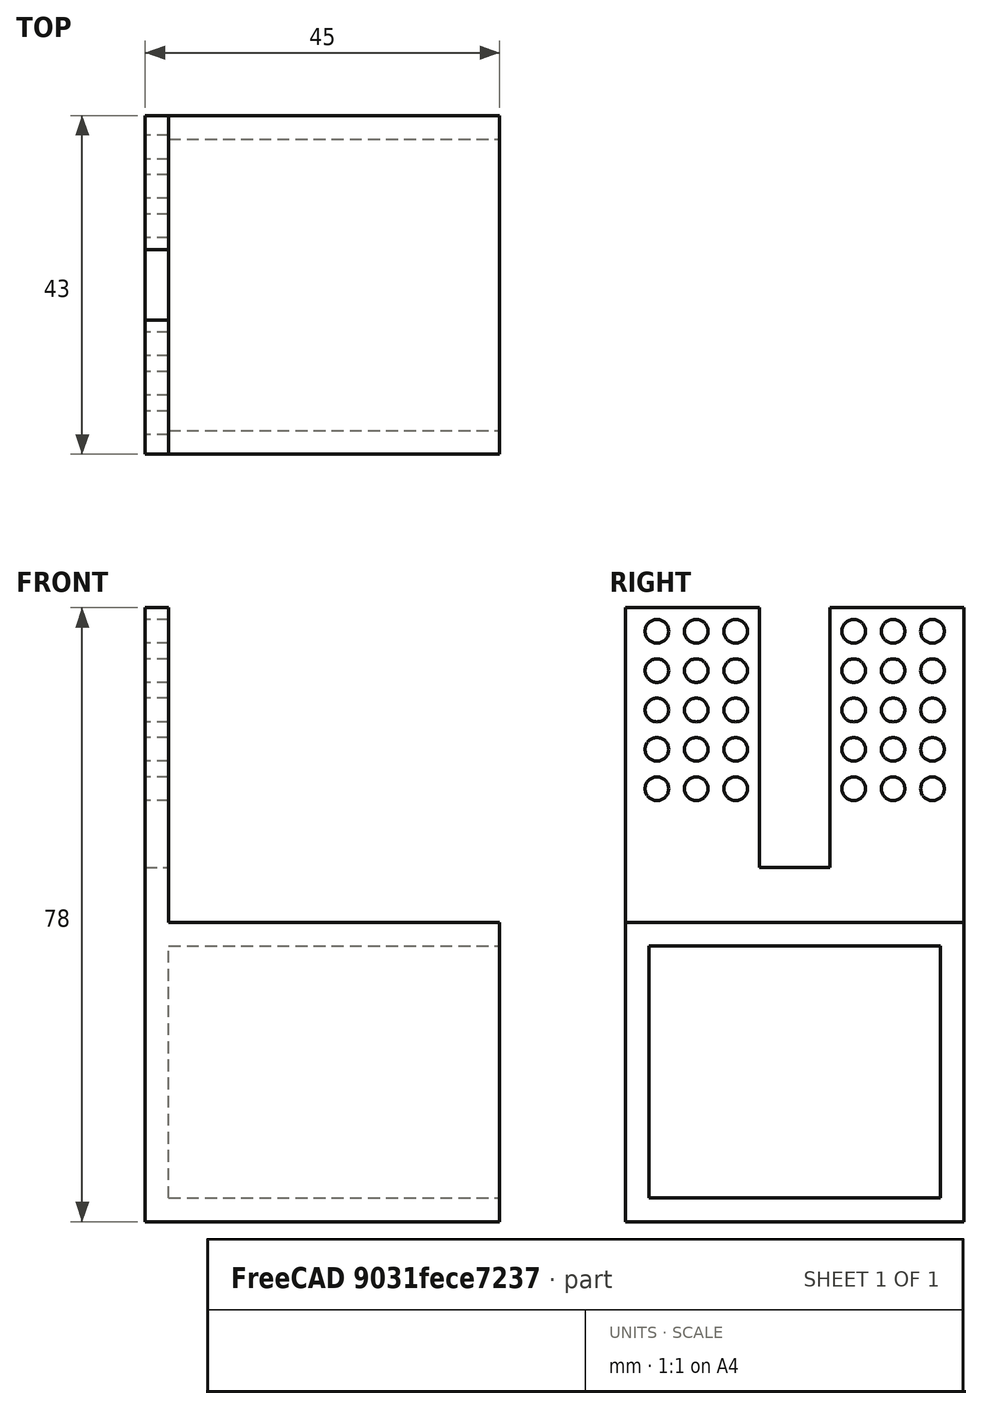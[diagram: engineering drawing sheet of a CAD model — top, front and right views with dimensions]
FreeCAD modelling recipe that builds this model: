
FCSTD DOCUMENT  (FreeCAD 0.14R3702 (Git))
Label: aWholeNewWorld
License: CC-BY 3.0
LicenseURL: http://creativecommons.org/licenses/by/3.0/
objects: Part::Cut×44, Part::Cylinder×41, Part::Box×5, Part::MultiFuse×1
note: 91 computed .brp shape members not serialized (recipe doc carries the construction recipe); baked Part::Feature solids carry a one-line shape summary decoded from their .brp

FEATURE [Part::Box] Box001  label="Cube001"
  Height = 38
  Length = 45
  Width = 43
FEATURE [Part::Box] Box  label="Cube"
  Height = 32
  Length = 42
  Placement = pos=(3,3,3) rot=(0,0,1;0rad)
  Width = 37
FEATURE [Part::Box] Box002  label="Cube002"
  Height = 40
  Length = 5
  Placement = pos=(0,0,38) rot=(0,0,1;0rad)
  Width = 43
FEATURE [Part::Cut] Cut
  Base = -> Box001
  Tool = -> Box
FEATURE [Part::Cylinder] Cylinder
  Angle = 360
  Height = 10
  Placement = pos=(7,9,70) rot=(0,-1,0;1.5708rad)
  Radius = 1.5
FEATURE [Part::Cylinder] Cylinder001
  Angle = 360
  Height = 10
  Placement = pos=(7,9,60) rot=(0,-1,0;1.5708rad)
  Radius = 1.5
FEATURE [Part::Cylinder] Cylinder002
  Angle = 360
  Height = 10
  Placement = pos=(7,19,70) rot=(0,-1,0;1.5708rad)
  Radius = 1.5
FEATURE [Part::Cylinder] Cylinder003
  Angle = 360
  Height = 10
  Placement = pos=(7,24,70) rot=(0,-1,0;1.5708rad)
  Radius = 1.5
FEATURE [Part::Cylinder] Cylinder004
  Angle = 360
  Height = 10
  Placement = pos=(7,4,70) rot=(0,-1,0;1.5708rad)
  Radius = 1.5
FEATURE [Part::Cylinder] Cylinder005
  Angle = 360
  Height = 10
  Placement = pos=(7,29,70) rot=(0,-1,0;1.5708rad)
  Radius = 1.5
FEATURE [Part::Cylinder] Cylinder006
  Angle = 360
  Height = 10
  Placement = pos=(7,34,70) rot=(0,-1,0;1.5708rad)
  Radius = 1.5
FEATURE [Part::Cylinder] Cylinder007
  Angle = 360
  Height = 10
  Placement = pos=(7,39,70) rot=(0,-1,0;1.5708rad)
  Radius = 1.5
FEATURE [Part::Cylinder] Cylinder008
  Angle = 360
  Height = 10
  Placement = pos=(7,4,65) rot=(0,-1,0;1.5708rad)
  Radius = 1.5
FEATURE [Part::Cylinder] Cylinder009
  Angle = 360
  Height = 10
  Placement = pos=(7,14,65) rot=(0,-1,0;1.5708rad)
  Radius = 1.5
FEATURE [Part::Cylinder] Cylinder010
  Angle = 360
  Height = 10
  Placement = pos=(7,19,65) rot=(0,-1,0;1.5708rad)
  Radius = 1.5
FEATURE [Part::Cylinder] Cylinder011
  Angle = 360
  Height = 10
  Placement = pos=(7,24,65) rot=(0,-1,0;1.5708rad)
  Radius = 1.5
FEATURE [Part::Cylinder] Cylinder012
  Angle = 360
  Height = 10
  Placement = pos=(7,4,65) rot=(0,-1,0;1.5708rad)
  Radius = 1.5
FEATURE [Part::Cylinder] Cylinder013
  Angle = 360
  Height = 10
  Placement = pos=(7,29,65) rot=(0,-1,0;1.5708rad)
  Radius = 1.5
FEATURE [Part::Cylinder] Cylinder014
  Angle = 360
  Height = 10
  Placement = pos=(7,34,65) rot=(0,-1,0;1.5708rad)
  Radius = 1.5
FEATURE [Part::Cylinder] Cylinder015
  Angle = 360
  Height = 10
  Placement = pos=(7,39,65) rot=(0,-1,0;1.5708rad)
  Radius = 1.5
FEATURE [Part::Cylinder] Cylinder016
  Angle = 360
  Height = 10
  Placement = pos=(7,9,65) rot=(0,-1,0;1.5708rad)
  Radius = 1.5
FEATURE [Part::Cut] Cut001
  Base = -> Box002
  Tool = -> Cylinder
FEATURE [Part::Cut] Cut002
  Base = -> Cut001
  Tool = -> Cylinder016
FEATURE [Part::Cut] Cut003
  Base = -> Cut002
  Tool = -> Cylinder015
FEATURE [Part::Cylinder] Cylinder017
  Angle = 360
  Height = 10
  Placement = pos=(7,14,60) rot=(0,-1,0;1.5708rad)
  Radius = 1.5
FEATURE [Part::Cylinder] Cylinder018
  Angle = 360
  Height = 10
  Placement = pos=(7,19,60) rot=(0,-1,0;1.5708rad)
  Radius = 1.5
FEATURE [Part::Cylinder] Cylinder019
  Angle = 360
  Height = 10
  Placement = pos=(7,24,60) rot=(0,-1,0;1.5708rad)
  Radius = 1.5
FEATURE [Part::Cylinder] Cylinder020
  Angle = 360
  Height = 10
  Placement = pos=(7,4,60) rot=(0,-1,0;1.5708rad)
  Radius = 1.5
FEATURE [Part::Cylinder] Cylinder021
  Angle = 360
  Height = 10
  Placement = pos=(7,29,60) rot=(0,-1,0;1.5708rad)
  Radius = 1.5
FEATURE [Part::Cylinder] Cylinder022
  Angle = 360
  Height = 10
  Placement = pos=(7,34,60) rot=(0,-1,0;1.5708rad)
  Radius = 1.5
FEATURE [Part::Cylinder] Cylinder023
  Angle = 360
  Height = 10
  Placement = pos=(7,39,60) rot=(0,-1,0;1.5708rad)
  Radius = 1.5
FEATURE [Part::Cylinder] Cylinder024
  Angle = 360
  Height = 10
  Placement = pos=(7,14,55) rot=(0,-1,0;1.5708rad)
  Radius = 1.5
FEATURE [Part::Cylinder] Cylinder025
  Angle = 360
  Height = 10
  Placement = pos=(7,19,55) rot=(0,-1,0;1.5708rad)
  Radius = 1.5
FEATURE [Part::Cylinder] Cylinder026
  Angle = 360
  Height = 10
  Placement = pos=(7,24,55) rot=(0,-1,0;1.5708rad)
  Radius = 1.5
FEATURE [Part::Cylinder] Cylinder027
  Angle = 360
  Height = 10
  Placement = pos=(7,4,55) rot=(0,-1,0;1.5708rad)
  Radius = 1.5
FEATURE [Part::Cylinder] Cylinder028
  Angle = 360
  Height = 10
  Placement = pos=(7,29,55) rot=(0,-1,0;1.5708rad)
  Radius = 1.5
FEATURE [Part::Cylinder] Cylinder029
  Angle = 360
  Height = 10
  Placement = pos=(7,34,55) rot=(0,-1,0;1.5708rad)
  Radius = 1.5
FEATURE [Part::Cylinder] Cylinder030
  Angle = 360
  Height = 10
  Placement = pos=(7,39,55) rot=(0,-1,0;1.5708rad)
  Radius = 1.5
FEATURE [Part::Cut] Cut004
  Base = -> Cut003
  Tool = -> Cylinder014
FEATURE [Part::Cut] Cut005
  Base = -> Cut004
  Tool = -> Cylinder030
FEATURE [Part::Cut] Cut006
  Base = -> Cut005
  Tool = -> Cylinder029
FEATURE [Part::Cut] Cut007
  Base = -> Cut006
  Tool = -> Cylinder028
FEATURE [Part::Cut] Cut008
  Base = -> Cut007
  Tool = -> Cylinder027
FEATURE [Part::Cut] Cut009
  Base = -> Cut008
  Tool = -> Cylinder026
FEATURE [Part::Cut] Cut010
  Base = -> Cut009
  Tool = -> Cylinder025
FEATURE [Part::Cut] Cut011
  Base = -> Cut010
  Tool = -> Cylinder024
FEATURE [Part::Cut] Cut012
  Base = -> Cut011
  Tool = -> Cylinder023
FEATURE [Part::Cut] Cut013
  Base = -> Cut012
  Tool = -> Cylinder022
FEATURE [Part::Cut] Cut014
  Base = -> Cut013
  Tool = -> Cylinder021
FEATURE [Part::Cut] Cut015
  Base = -> Cut014
  Tool = -> Cylinder020
FEATURE [Part::Cut] Cut016
  Base = -> Cut015
  Tool = -> Cylinder019
FEATURE [Part::Cut] Cut017
  Base = -> Cut016
  Tool = -> Cylinder018
FEATURE [Part::Cut] Cut018
  Base = -> Cut017
  Tool = -> Cylinder017
FEATURE [Part::Cut] Cut019
  Base = -> Cut018
  Tool = -> Cylinder013
FEATURE [Part::Cut] Cut020
  Base = -> Cut019
  Tool = -> Cylinder012
FEATURE [Part::Cut] Cut021
  Base = -> Cut020
  Tool = -> Cylinder011
FEATURE [Part::Cut] Cut022
  Base = -> Cut021
  Tool = -> Cylinder010
FEATURE [Part::Cut] Cut023
  Base = -> Cut022
  Tool = -> Cylinder009
FEATURE [Part::Cut] Cut024
  Base = -> Cut023
  Tool = -> Cylinder008
FEATURE [Part::Cut] Cut025
  Base = -> Cut024
  Tool = -> Cylinder007
FEATURE [Part::Cut] Cut026
  Base = -> Cut025
  Tool = -> Cylinder006
FEATURE [Part::Cut] Cut027
  Base = -> Cut026
  Tool = -> Cylinder005
FEATURE [Part::Cut] Cut028
  Base = -> Cut027
  Tool = -> Cylinder004
FEATURE [Part::Cut] Cut029
  Base = -> Cut028
  Tool = -> Cylinder003
FEATURE [Part::Cut] Cut030
  Base = -> Cut029
  Tool = -> Cylinder002
FEATURE [Part::Cylinder] Cylinder031
  Angle = 360
  Height = 10
  Placement = pos=(7,14,70) rot=(0,-1,0;1.5708rad)
  Radius = 1.5
FEATURE [Part::Cylinder] Cylinder032
  Angle = 360
  Height = 10
  Placement = pos=(7,9,55) rot=(0,-1,0;1.5708rad)
  Radius = 1.5
FEATURE [Part::Cut] Cut031
  Base = -> Cut030
  Tool = -> Cylinder001
FEATURE [Part::Cut] Cut032
  Base = -> Cut031
  Tool = -> Cylinder032
FEATURE [Part::Cut] Cut033
  Base = -> Cut032
  Tool = -> Cylinder031
FEATURE [Part::Box] Box003  label="Cube003"
  Height = 40
  Length = 2
  Placement = pos=(3,0,38) rot=(0,0,1;0rad)
  Width = 43
FEATURE [Part::Cut] Cut034
  Base = -> Cut033
  Tool = -> Box003
FEATURE [Part::MultiFuse] Fusion
  Shapes = -> [Cut,Cut034]
FEATURE [Part::Cylinder] Cylinder033 .. Cylinder040  x8 (patterned run collapsed; names and placements below)
  Angle = 360
  Height = 10
  Radius = 1.5
  placements: 8 in arithmetic series — first pos=(5,4,75) rot=(0,-1,0;1.5708rad), step (0,5,0), last pos=(5,39,75) rot=(0,-1,0;1.5708rad)
FEATURE [Part::Cut] Cut035
  Base = -> Fusion
  Tool = -> Cylinder033
FEATURE [Part::Cut] Cut036
  Base = -> Cut035
  Tool = -> Cylinder040
FEATURE [Part::Cut] Cut037
  Base = -> Cut036
  Tool = -> Cylinder039
FEATURE [Part::Cut] Cut038
  Base = -> Cut037
  Tool = -> Cylinder038
FEATURE [Part::Cut] Cut039
  Base = -> Cut038
  Tool = -> Cylinder037
FEATURE [Part::Cut] Cut040
  Base = -> Cut039
  Tool = -> Cylinder036
FEATURE [Part::Cut] Cut041
  Base = -> Cut040
  Tool = -> Cylinder035
FEATURE [Part::Cut] Cut042
  Base = -> Cut041
  Tool = -> Cylinder034
FEATURE [Part::Box] Box004  label="Cube004"
  Height = 33
  Length = 3
  Placement = pos=(0,17,45) rot=(0,0,1;0rad)
  Width = 9
FEATURE [Part::Cut] Cut043
  Base = -> Cut042
  Tool = -> Box004
